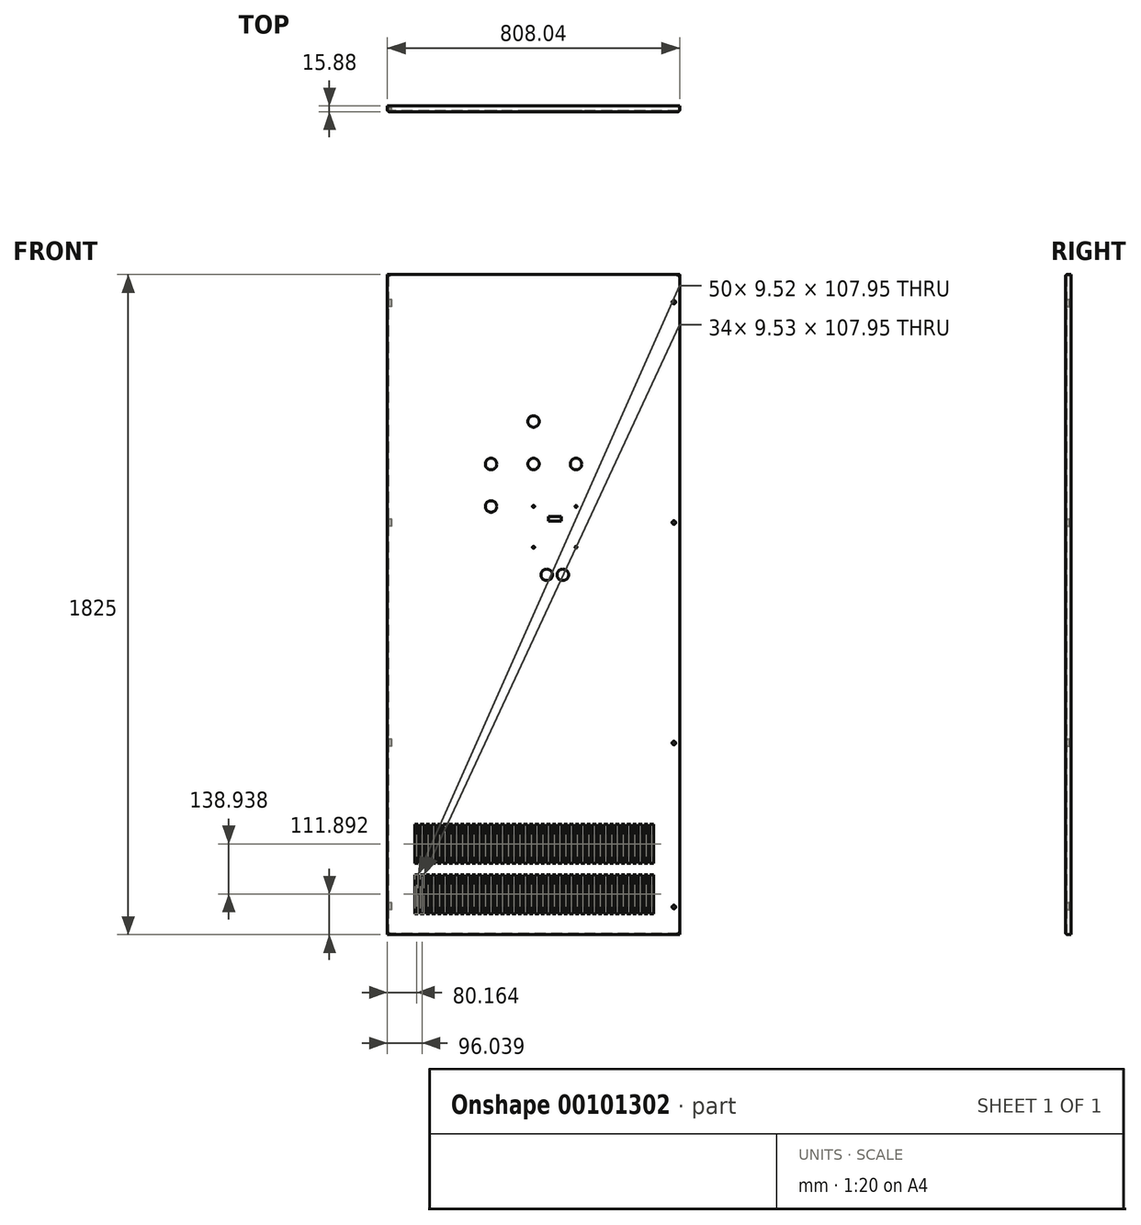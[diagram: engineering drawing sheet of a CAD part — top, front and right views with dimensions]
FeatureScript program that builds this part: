
annotation { "Feature Type Name" : "Feature", "Feature Type Description" : "" }
export const myFeature = defineFeature(function(context is Context, id is Id, definition is map)
    precondition{}
    {
        {
            var Q0;
            Q0=qCreatedBy(makeId("Front.planeOp"),FACE);
            var sketch = newSketch(context, id + "F0", { "sketchPlane" : qUnion([Q0])});
            skLineSegment(sketch, "E0.bottom", {"start": v(404.02, 912.5) * mm, "end": v(-404.02, 912.5) * mm});
            skLineSegment(sketch, "E0.top", {"start": v(404.02, -912.5) * mm, "end": v(-404.02, -912.5) * mm});
            skLineSegment(sketch, "E0.left", {"start": v(404.02, 912.5) * mm, "end": v(404.02, -912.5) * mm});
            skLineSegment(sketch, "E0.right", {"start": v(-404.02, 912.5) * mm, "end": v(-404.02, -912.5) * mm});
            skPoint(sketch, "E0.middle", {"position": v(0, 0) * mm});
            skSolve(sketch);
        }
        {
            var Q0;
            Q0=makeQuery(id+"F0.imprint","IMPRINT",FACE,{"disambiguationData":[TD([[makeQuery(id+"F0.imprint","IMPRINT",EDGE,{"derivedFrom":sQuery(id+"F0.wireOp",EDGE,"E0.bottom")}),1.0]])]});
            var Q1;
            Q1=qSketchRegion(id+"F0",true);
            extrude(context, id + "F1", {"entities" : qUnion([Q0, Q1]), "endBound" : BoundingType.SYMMETRIC, "depth" : 15.88 * mm});
        }
        {
            var Q0;
            Q0=makeQuery(id+"F1.opExtrude","CAP_FACE",FACE,{"disambiguationData":[OSD([sQuery(id+"F0.wireOp",EDGE,"E0.bottom"),sQuery(id+"F0.wireOp",EDGE,"E0.top"),sQuery(id+"F0.wireOp",EDGE,"E0.left"),sQuery(id+"F0.wireOp",EDGE,"E0.right")])],"isStart":true});
            shell(context, id + "F2", {"entities" : qUnion([Q0]), "thickness" : 2.66 * mm});
        }
        {
            var Q0;
            Q0=makeQuery(id+"F1.opExtrude","CAP_EDGE",EDGE,{"disambiguationData":[OSD([sQuery(id+"F0.wireOp",EDGE,"E0.bottom")])],"isStart":false});
            var Q1;
            Q1=makeQuery(id+"F1.opExtrude","CAP_EDGE",EDGE,{"disambiguationData":[OSD([sQuery(id+"F0.wireOp",EDGE,"E0.left")])],"isStart":false});
            var Q2;
            Q2=makeQuery(id+"F1.opExtrude","CAP_EDGE",EDGE,{"disambiguationData":[OSD([sQuery(id+"F0.wireOp",EDGE,"E0.right")])],"isStart":false});
            var Q3;
            Q3=makeQuery(id+"F1.opExtrude","CAP_EDGE",EDGE,{"disambiguationData":[OSD([sQuery(id+"F0.wireOp",EDGE,"E0.top")])],"isStart":false});
            fillet(context, id + "F3", {"entities" : qUnion([Q0, Q1, Q2, Q3]), "radius" : 5.08 * mm, "tangentPropagation" : true, "allowEdgeOverflow" : false});
        }
        {
            var Q0;
            Q0=makeQuery(id+"F1.opExtrude","CAP_FACE",FACE,{"disambiguationData":[OSD([sQuery(id+"F0.wireOp",EDGE,"E0.bottom"),sQuery(id+"F0.wireOp",EDGE,"E0.top"),sQuery(id+"F0.wireOp",EDGE,"E0.left"),sQuery(id+"F0.wireOp",EDGE,"E0.right")])],"isStart":false});
            var sketch = newSketch(context, id + "F4", { "sketchPlane" : qUnion([Q0])});
            skCircle(sketch, "E1", {"center": v(388.14, 836.3) * mm, "radius": 4.76 * mm});
            skCircle(sketch, "E2", {"center": v(388.14, -382.9) * mm, "radius": 4.76 * mm});
            skCircle(sketch, "E3", {"center": v(388.14, -836.3) * mm, "radius": 4.76 * mm});
            skLineSegment(sketch, "E4.bottom", {"start": v(322.26, -854.58) * mm, "end": v(331.78, -854.58) * mm});
            skLineSegment(sketch, "E4.top", {"start": v(322.26, -746.63) * mm, "end": v(331.78, -746.63) * mm});
            skLineSegment(sketch, "E4.left", {"start": v(322.26, -854.58) * mm, "end": v(322.26, -746.63) * mm});
            skLineSegment(sketch, "E4.right", {"start": v(331.78, -854.58) * mm, "end": v(331.78, -746.63) * mm});
            skLineSegment(sketch, "E5.1.0.0", {"start": v(315.9, -854.58) * mm, "end": v(315.9, -746.63) * mm});
            skLineSegment(sketch, "E5.1.0.1", {"start": v(306.38, -854.58) * mm, "end": v(306.38, -746.63) * mm});
            skLineSegment(sketch, "E5.1.0.2", {"start": v(306.38, -854.58) * mm, "end": v(315.9, -854.58) * mm});
            skLineSegment(sketch, "E5.1.0.3", {"start": v(306.38, -746.63) * mm, "end": v(315.9, -746.63) * mm});
            skLineSegment(sketch, "E5.2.0.0", {"start": v(300.03, -854.58) * mm, "end": v(300.03, -746.63) * mm});
            skLineSegment(sketch, "E5.2.0.1", {"start": v(290.5, -854.58) * mm, "end": v(290.5, -746.63) * mm});
            skLineSegment(sketch, "E5.2.0.2", {"start": v(290.5, -854.58) * mm, "end": v(300.03, -854.58) * mm});
            skLineSegment(sketch, "E5.2.0.3", {"start": v(290.5, -746.63) * mm, "end": v(300.03, -746.63) * mm});
            skLineSegment(sketch, "E5.3.0.0", {"start": v(284.16, -854.58) * mm, "end": v(284.16, -746.63) * mm});
            skLineSegment(sketch, "E5.3.0.1", {"start": v(274.63, -854.58) * mm, "end": v(274.63, -746.63) * mm});
            skLineSegment(sketch, "E5.3.0.2", {"start": v(274.63, -854.58) * mm, "end": v(284.16, -854.58) * mm});
            skLineSegment(sketch, "E5.3.0.3", {"start": v(274.63, -746.63) * mm, "end": v(284.16, -746.63) * mm});
            skLineSegment(sketch, "E5.4.0.0", {"start": v(268.28, -854.58) * mm, "end": v(268.28, -746.63) * mm});
            skLineSegment(sketch, "E5.4.0.1", {"start": v(258.76, -854.58) * mm, "end": v(258.76, -746.63) * mm});
            skLineSegment(sketch, "E5.4.0.2", {"start": v(258.76, -854.58) * mm, "end": v(268.28, -854.58) * mm});
            skLineSegment(sketch, "E5.4.0.3", {"start": v(258.76, -746.63) * mm, "end": v(268.28, -746.63) * mm});
            skLineSegment(sketch, "E5.5.0.0", {"start": v(252.4, -854.58) * mm, "end": v(252.4, -746.63) * mm});
            skLineSegment(sketch, "E5.5.0.1", {"start": v(242.88, -854.58) * mm, "end": v(242.88, -746.63) * mm});
            skLineSegment(sketch, "E5.5.0.2", {"start": v(242.88, -854.58) * mm, "end": v(252.4, -854.58) * mm});
            skLineSegment(sketch, "E5.5.0.3", {"start": v(242.88, -746.63) * mm, "end": v(252.4, -746.63) * mm});
            skLineSegment(sketch, "E5.6.0.0", {"start": v(236.53, -854.58) * mm, "end": v(236.53, -746.63) * mm});
            skLineSegment(sketch, "E5.6.0.1", {"start": v(227, -854.58) * mm, "end": v(227, -746.63) * mm});
            skLineSegment(sketch, "E5.6.0.2", {"start": v(227, -854.58) * mm, "end": v(236.53, -854.58) * mm});
            skLineSegment(sketch, "E5.6.0.3", {"start": v(227, -746.63) * mm, "end": v(236.53, -746.63) * mm});
            skLineSegment(sketch, "E5.7.0.0", {"start": v(220.66, -854.58) * mm, "end": v(220.66, -746.63) * mm});
            skLineSegment(sketch, "E5.7.0.1", {"start": v(211.13, -854.58) * mm, "end": v(211.13, -746.63) * mm});
            skLineSegment(sketch, "E5.7.0.2", {"start": v(211.13, -854.58) * mm, "end": v(220.66, -854.58) * mm});
            skLineSegment(sketch, "E5.7.0.3", {"start": v(211.13, -746.63) * mm, "end": v(220.66, -746.63) * mm});
            skLineSegment(sketch, "E5.8.0.0", {"start": v(204.78, -854.58) * mm, "end": v(204.78, -746.63) * mm});
            skLineSegment(sketch, "E5.8.0.1", {"start": v(195.26, -854.58) * mm, "end": v(195.26, -746.63) * mm});
            skLineSegment(sketch, "E5.8.0.2", {"start": v(195.26, -854.58) * mm, "end": v(204.78, -854.58) * mm});
            skLineSegment(sketch, "E5.8.0.3", {"start": v(195.26, -746.63) * mm, "end": v(204.78, -746.63) * mm});
            skLineSegment(sketch, "E5.9.0.0", {"start": v(188.9, -854.58) * mm, "end": v(188.9, -746.63) * mm});
            skLineSegment(sketch, "E5.9.0.1", {"start": v(179.38, -854.58) * mm, "end": v(179.38, -746.63) * mm});
            skLineSegment(sketch, "E5.9.0.2", {"start": v(179.38, -854.58) * mm, "end": v(188.9, -854.58) * mm});
            skLineSegment(sketch, "E5.9.0.3", {"start": v(179.38, -746.63) * mm, "end": v(188.9, -746.63) * mm});
            skLineSegment(sketch, "E5.10.0.0", {"start": v(173.03, -854.58) * mm, "end": v(173.03, -746.63) * mm});
            skLineSegment(sketch, "E5.10.0.1", {"start": v(163.5, -854.58) * mm, "end": v(163.5, -746.63) * mm});
            skLineSegment(sketch, "E5.10.0.2", {"start": v(163.5, -854.58) * mm, "end": v(173.03, -854.58) * mm});
            skLineSegment(sketch, "E5.10.0.3", {"start": v(163.5, -746.63) * mm, "end": v(173.03, -746.63) * mm});
            skLineSegment(sketch, "E5.11.0.0", {"start": v(157.16, -854.58) * mm, "end": v(157.16, -746.63) * mm});
            skLineSegment(sketch, "E5.11.0.1", {"start": v(147.63, -854.58) * mm, "end": v(147.63, -746.63) * mm});
            skLineSegment(sketch, "E5.11.0.2", {"start": v(147.63, -854.58) * mm, "end": v(157.16, -854.58) * mm});
            skLineSegment(sketch, "E5.11.0.3", {"start": v(147.63, -746.63) * mm, "end": v(157.16, -746.63) * mm});
            skLineSegment(sketch, "E5.12.0.0", {"start": v(141.28, -854.58) * mm, "end": v(141.28, -746.63) * mm});
            skLineSegment(sketch, "E5.12.0.1", {"start": v(131.76, -854.58) * mm, "end": v(131.76, -746.63) * mm});
            skLineSegment(sketch, "E5.12.0.2", {"start": v(131.76, -854.58) * mm, "end": v(141.28, -854.58) * mm});
            skLineSegment(sketch, "E5.12.0.3", {"start": v(131.76, -746.63) * mm, "end": v(141.28, -746.63) * mm});
            skLineSegment(sketch, "E5.13.0.0", {"start": v(125.4, -854.58) * mm, "end": v(125.4, -746.63) * mm});
            skLineSegment(sketch, "E5.13.0.1", {"start": v(115.88, -854.58) * mm, "end": v(115.88, -746.63) * mm});
            skLineSegment(sketch, "E5.13.0.2", {"start": v(115.88, -854.58) * mm, "end": v(125.4, -854.58) * mm});
            skLineSegment(sketch, "E5.13.0.3", {"start": v(115.88, -746.63) * mm, "end": v(125.4, -746.63) * mm});
            skLineSegment(sketch, "E5.14.0.0", {"start": v(109.53, -854.58) * mm, "end": v(109.53, -746.63) * mm});
            skLineSegment(sketch, "E5.14.0.1", {"start": v(100, -854.58) * mm, "end": v(100, -746.63) * mm});
            skLineSegment(sketch, "E5.14.0.2", {"start": v(100, -854.58) * mm, "end": v(109.53, -854.58) * mm});
            skLineSegment(sketch, "E5.14.0.3", {"start": v(100, -746.63) * mm, "end": v(109.53, -746.63) * mm});
            skLineSegment(sketch, "E5.15.0.0", {"start": v(93.66, -854.58) * mm, "end": v(93.66, -746.63) * mm});
            skLineSegment(sketch, "E5.15.0.1", {"start": v(84.13, -854.58) * mm, "end": v(84.13, -746.63) * mm});
            skLineSegment(sketch, "E5.15.0.2", {"start": v(84.13, -854.58) * mm, "end": v(93.66, -854.58) * mm});
            skLineSegment(sketch, "E5.15.0.3", {"start": v(84.13, -746.63) * mm, "end": v(93.66, -746.63) * mm});
            skLineSegment(sketch, "E5.16.0.0", {"start": v(77.78, -854.58) * mm, "end": v(77.78, -746.63) * mm});
            skLineSegment(sketch, "E5.16.0.1", {"start": v(68.26, -854.58) * mm, "end": v(68.26, -746.63) * mm});
            skLineSegment(sketch, "E5.16.0.2", {"start": v(68.26, -854.58) * mm, "end": v(77.78, -854.58) * mm});
            skLineSegment(sketch, "E5.16.0.3", {"start": v(68.26, -746.63) * mm, "end": v(77.78, -746.63) * mm});
            skLineSegment(sketch, "E5.17.0.0", {"start": v(61.9, -854.58) * mm, "end": v(61.9, -746.63) * mm});
            skLineSegment(sketch, "E5.17.0.1", {"start": v(52.38, -854.58) * mm, "end": v(52.38, -746.63) * mm});
            skLineSegment(sketch, "E5.17.0.2", {"start": v(52.38, -854.58) * mm, "end": v(61.9, -854.58) * mm});
            skLineSegment(sketch, "E5.17.0.3", {"start": v(52.38, -746.63) * mm, "end": v(61.9, -746.63) * mm});
            skLineSegment(sketch, "E5.18.0.0", {"start": v(46.03, -854.58) * mm, "end": v(46.03, -746.63) * mm});
            skLineSegment(sketch, "E5.18.0.1", {"start": v(36.5, -854.58) * mm, "end": v(36.5, -746.63) * mm});
            skLineSegment(sketch, "E5.18.0.2", {"start": v(36.5, -854.58) * mm, "end": v(46.03, -854.58) * mm});
            skLineSegment(sketch, "E5.18.0.3", {"start": v(36.5, -746.63) * mm, "end": v(46.03, -746.63) * mm});
            skLineSegment(sketch, "E5.19.0.0", {"start": v(30.16, -854.58) * mm, "end": v(30.16, -746.63) * mm});
            skLineSegment(sketch, "E5.19.0.1", {"start": v(20.63, -854.58) * mm, "end": v(20.63, -746.63) * mm});
            skLineSegment(sketch, "E5.19.0.2", {"start": v(20.63, -854.58) * mm, "end": v(30.16, -854.58) * mm});
            skLineSegment(sketch, "E5.19.0.3", {"start": v(20.63, -746.63) * mm, "end": v(30.16, -746.63) * mm});
            skLineSegment(sketch, "E5.20.0.0", {"start": v(14.28, -854.58) * mm, "end": v(14.28, -746.63) * mm});
            skLineSegment(sketch, "E5.20.0.1", {"start": v(4.76, -854.58) * mm, "end": v(4.76, -746.63) * mm});
            skLineSegment(sketch, "E5.20.0.2", {"start": v(4.76, -854.58) * mm, "end": v(14.28, -854.58) * mm});
            skLineSegment(sketch, "E5.20.0.3", {"start": v(4.76, -746.63) * mm, "end": v(14.28, -746.63) * mm});
            skLineSegment(sketch, "E5.21.0.0", {"start": v(-1.6, -854.58) * mm, "end": v(-1.6, -746.63) * mm});
            skLineSegment(sketch, "E5.21.0.1", {"start": v(-11.12, -854.58) * mm, "end": v(-11.12, -746.63) * mm});
            skLineSegment(sketch, "E5.21.0.2", {"start": v(-11.12, -854.58) * mm, "end": v(-1.6, -854.58) * mm});
            skLineSegment(sketch, "E5.21.0.3", {"start": v(-11.12, -746.63) * mm, "end": v(-1.6, -746.63) * mm});
            skLineSegment(sketch, "E5.22.0.0", {"start": v(-17.47, -854.58) * mm, "end": v(-17.47, -746.63) * mm});
            skLineSegment(sketch, "E5.22.0.1", {"start": v(-27, -854.58) * mm, "end": v(-27, -746.63) * mm});
            skLineSegment(sketch, "E5.22.0.2", {"start": v(-27, -854.58) * mm, "end": v(-17.47, -854.58) * mm});
            skLineSegment(sketch, "E5.22.0.3", {"start": v(-27, -746.63) * mm, "end": v(-17.47, -746.63) * mm});
            skLineSegment(sketch, "E5.23.0.0", {"start": v(-33.34, -854.58) * mm, "end": v(-33.34, -746.63) * mm});
            skLineSegment(sketch, "E5.23.0.1", {"start": v(-42.87, -854.58) * mm, "end": v(-42.87, -746.63) * mm});
            skLineSegment(sketch, "E5.23.0.2", {"start": v(-42.87, -854.58) * mm, "end": v(-33.34, -854.58) * mm});
            skLineSegment(sketch, "E5.23.0.3", {"start": v(-42.87, -746.63) * mm, "end": v(-33.34, -746.63) * mm});
            skLineSegment(sketch, "E5.24.0.0", {"start": v(-49.22, -854.58) * mm, "end": v(-49.22, -746.63) * mm});
            skLineSegment(sketch, "E5.24.0.1", {"start": v(-58.74, -854.58) * mm, "end": v(-58.74, -746.63) * mm});
            skLineSegment(sketch, "E5.24.0.2", {"start": v(-58.74, -854.58) * mm, "end": v(-49.22, -854.58) * mm});
            skLineSegment(sketch, "E5.24.0.3", {"start": v(-58.74, -746.63) * mm, "end": v(-49.22, -746.63) * mm});
            skLineSegment(sketch, "E5.25.0.0", {"start": v(-65.1, -854.58) * mm, "end": v(-65.1, -746.63) * mm});
            skLineSegment(sketch, "E5.25.0.1", {"start": v(-74.62, -854.58) * mm, "end": v(-74.62, -746.63) * mm});
            skLineSegment(sketch, "E5.25.0.2", {"start": v(-74.62, -854.58) * mm, "end": v(-65.1, -854.58) * mm});
            skLineSegment(sketch, "E5.25.0.3", {"start": v(-74.62, -746.63) * mm, "end": v(-65.1, -746.63) * mm});
            skLineSegment(sketch, "E5.26.0.0", {"start": v(-80.97, -854.58) * mm, "end": v(-80.97, -746.63) * mm});
            skLineSegment(sketch, "E5.26.0.1", {"start": v(-90.5, -854.58) * mm, "end": v(-90.5, -746.63) * mm});
            skLineSegment(sketch, "E5.26.0.2", {"start": v(-90.5, -854.58) * mm, "end": v(-80.97, -854.58) * mm});
            skLineSegment(sketch, "E5.26.0.3", {"start": v(-90.5, -746.63) * mm, "end": v(-80.97, -746.63) * mm});
            skLineSegment(sketch, "E5.27.0.0", {"start": v(-96.84, -854.58) * mm, "end": v(-96.84, -746.63) * mm});
            skLineSegment(sketch, "E5.27.0.1", {"start": v(-106.37, -854.58) * mm, "end": v(-106.37, -746.63) * mm});
            skLineSegment(sketch, "E5.27.0.2", {"start": v(-106.37, -854.58) * mm, "end": v(-96.84, -854.58) * mm});
            skLineSegment(sketch, "E5.27.0.3", {"start": v(-106.37, -746.63) * mm, "end": v(-96.84, -746.63) * mm});
            skLineSegment(sketch, "E5.28.0.0", {"start": v(-112.72, -854.58) * mm, "end": v(-112.72, -746.63) * mm});
            skLineSegment(sketch, "E5.28.0.1", {"start": v(-122.24, -854.58) * mm, "end": v(-122.24, -746.63) * mm});
            skLineSegment(sketch, "E5.28.0.2", {"start": v(-122.24, -854.58) * mm, "end": v(-112.72, -854.58) * mm});
            skLineSegment(sketch, "E5.28.0.3", {"start": v(-122.24, -746.63) * mm, "end": v(-112.72, -746.63) * mm});
            skLineSegment(sketch, "E5.29.0.0", {"start": v(-128.6, -854.58) * mm, "end": v(-128.6, -746.63) * mm});
            skLineSegment(sketch, "E5.29.0.1", {"start": v(-138.12, -854.58) * mm, "end": v(-138.12, -746.63) * mm});
            skLineSegment(sketch, "E5.29.0.2", {"start": v(-138.12, -854.58) * mm, "end": v(-128.6, -854.58) * mm});
            skLineSegment(sketch, "E5.29.0.3", {"start": v(-138.12, -746.63) * mm, "end": v(-128.6, -746.63) * mm});
            skLineSegment(sketch, "E5.30.0.0", {"start": v(-144.47, -854.58) * mm, "end": v(-144.47, -746.63) * mm});
            skLineSegment(sketch, "E5.30.0.1", {"start": v(-154, -854.58) * mm, "end": v(-154, -746.63) * mm});
            skLineSegment(sketch, "E5.30.0.2", {"start": v(-154, -854.58) * mm, "end": v(-144.47, -854.58) * mm});
            skLineSegment(sketch, "E5.30.0.3", {"start": v(-154, -746.63) * mm, "end": v(-144.47, -746.63) * mm});
            skLineSegment(sketch, "E5.31.0.0", {"start": v(-160.34, -854.58) * mm, "end": v(-160.34, -746.63) * mm});
            skLineSegment(sketch, "E5.31.0.1", {"start": v(-169.87, -854.58) * mm, "end": v(-169.87, -746.63) * mm});
            skLineSegment(sketch, "E5.31.0.2", {"start": v(-169.87, -854.58) * mm, "end": v(-160.34, -854.58) * mm});
            skLineSegment(sketch, "E5.31.0.3", {"start": v(-169.87, -746.63) * mm, "end": v(-160.34, -746.63) * mm});
            skLineSegment(sketch, "E5.32.0.0", {"start": v(-176.22, -854.58) * mm, "end": v(-176.22, -746.63) * mm});
            skLineSegment(sketch, "E5.32.0.1", {"start": v(-185.74, -854.58) * mm, "end": v(-185.74, -746.63) * mm});
            skLineSegment(sketch, "E5.32.0.2", {"start": v(-185.74, -854.58) * mm, "end": v(-176.22, -854.58) * mm});
            skLineSegment(sketch, "E5.32.0.3", {"start": v(-185.74, -746.63) * mm, "end": v(-176.22, -746.63) * mm});
            skLineSegment(sketch, "E5.33.0.0", {"start": v(-192.1, -854.58) * mm, "end": v(-192.1, -746.63) * mm});
            skLineSegment(sketch, "E5.33.0.1", {"start": v(-201.62, -854.58) * mm, "end": v(-201.62, -746.63) * mm});
            skLineSegment(sketch, "E5.33.0.2", {"start": v(-201.62, -854.58) * mm, "end": v(-192.1, -854.58) * mm});
            skLineSegment(sketch, "E5.33.0.3", {"start": v(-201.62, -746.63) * mm, "end": v(-192.1, -746.63) * mm});
            skLineSegment(sketch, "E5.direction1", {"start": v(331.78, -854.58) * mm, "end": v(315.9, -854.58) * mm, "construction": true});
            skLineSegment(sketch, "E5.direction2", {"start": v(331.78, -854.58) * mm, "end": v(331.78, -715.65) * mm, "construction": true});
            skLineSegment(sketch, "E6.0.34.0", {"start": v(-207.97, -854.58) * mm, "end": v(-207.97, -746.63) * mm});
            skLineSegment(sketch, "E6.3.34.0", {"start": v(-217.5, -854.58) * mm, "end": v(-217.5, -746.63) * mm});
            skLineSegment(sketch, "E6.6.34.0", {"start": v(-217.5, -854.58) * mm, "end": v(-207.97, -854.58) * mm});
            skLineSegment(sketch, "E6.9.34.0", {"start": v(-217.5, -746.63) * mm, "end": v(-207.97, -746.63) * mm});
            skLineSegment(sketch, "E6.0.35.0", {"start": v(-223.84, -854.58) * mm, "end": v(-223.84, -746.63) * mm});
            skLineSegment(sketch, "E6.3.35.0", {"start": v(-233.37, -854.58) * mm, "end": v(-233.37, -746.63) * mm});
            skLineSegment(sketch, "E6.6.35.0", {"start": v(-233.37, -854.58) * mm, "end": v(-223.84, -854.58) * mm});
            skLineSegment(sketch, "E6.9.35.0", {"start": v(-233.37, -746.63) * mm, "end": v(-223.84, -746.63) * mm});
            skLineSegment(sketch, "E6.0.36.0", {"start": v(-239.72, -854.58) * mm, "end": v(-239.72, -746.63) * mm});
            skLineSegment(sketch, "E6.3.36.0", {"start": v(-249.24, -854.58) * mm, "end": v(-249.24, -746.63) * mm});
            skLineSegment(sketch, "E6.6.36.0", {"start": v(-249.24, -854.58) * mm, "end": v(-239.72, -854.58) * mm});
            skLineSegment(sketch, "E6.9.36.0", {"start": v(-249.24, -746.63) * mm, "end": v(-239.72, -746.63) * mm});
            skLineSegment(sketch, "E6.0.37.0", {"start": v(-255.6, -854.58) * mm, "end": v(-255.6, -746.63) * mm});
            skLineSegment(sketch, "E6.3.37.0", {"start": v(-265.12, -854.58) * mm, "end": v(-265.12, -746.63) * mm});
            skLineSegment(sketch, "E6.6.37.0", {"start": v(-265.12, -854.58) * mm, "end": v(-255.6, -854.58) * mm});
            skLineSegment(sketch, "E6.9.37.0", {"start": v(-265.12, -746.63) * mm, "end": v(-255.6, -746.63) * mm});
            skLineSegment(sketch, "E6.0.38.0", {"start": v(-271.47, -854.58) * mm, "end": v(-271.47, -746.63) * mm});
            skLineSegment(sketch, "E6.3.38.0", {"start": v(-281, -854.58) * mm, "end": v(-281, -746.63) * mm});
            skLineSegment(sketch, "E6.6.38.0", {"start": v(-281, -854.58) * mm, "end": v(-271.47, -854.58) * mm});
            skLineSegment(sketch, "E6.9.38.0", {"start": v(-281, -746.63) * mm, "end": v(-271.47, -746.63) * mm});
            skLineSegment(sketch, "E6.0.39.0", {"start": v(-287.34, -854.58) * mm, "end": v(-287.34, -746.63) * mm});
            skLineSegment(sketch, "E6.3.39.0", {"start": v(-296.87, -854.58) * mm, "end": v(-296.87, -746.63) * mm});
            skLineSegment(sketch, "E6.6.39.0", {"start": v(-296.87, -854.58) * mm, "end": v(-287.34, -854.58) * mm});
            skLineSegment(sketch, "E6.9.39.0", {"start": v(-296.87, -746.63) * mm, "end": v(-287.34, -746.63) * mm});
            skLineSegment(sketch, "E6.0.40.0", {"start": v(-303.22, -854.58) * mm, "end": v(-303.22, -746.63) * mm});
            skLineSegment(sketch, "E6.3.40.0", {"start": v(-312.74, -854.58) * mm, "end": v(-312.74, -746.63) * mm});
            skLineSegment(sketch, "E6.6.40.0", {"start": v(-312.74, -854.58) * mm, "end": v(-303.22, -854.58) * mm});
            skLineSegment(sketch, "E6.9.40.0", {"start": v(-312.74, -746.63) * mm, "end": v(-303.22, -746.63) * mm});
            skLineSegment(sketch, "E6.0.41.0", {"start": v(-319.1, -854.58) * mm, "end": v(-319.1, -746.63) * mm});
            skLineSegment(sketch, "E6.3.41.0", {"start": v(-328.62, -854.58) * mm, "end": v(-328.62, -746.63) * mm});
            skLineSegment(sketch, "E6.6.41.0", {"start": v(-328.62, -854.58) * mm, "end": v(-319.1, -854.58) * mm});
            skLineSegment(sketch, "E6.9.41.0", {"start": v(-328.62, -746.63) * mm, "end": v(-319.1, -746.63) * mm});
            skLineSegment(sketch, "E7.direction1", {"start": v(-281, -854.58) * mm, "end": v(-259.44, -854.58) * mm, "construction": true});
            skLineSegment(sketch, "E8.0.0.1", {"start": v(331.78, -715.65) * mm, "end": v(331.78, -607.7) * mm});
            skLineSegment(sketch, "E8.3.0.1", {"start": v(322.26, -715.65) * mm, "end": v(322.26, -607.7) * mm});
            skLineSegment(sketch, "E8.6.0.1", {"start": v(322.26, -715.65) * mm, "end": v(331.78, -715.65) * mm});
            skLineSegment(sketch, "E8.9.0.1", {"start": v(322.26, -607.7) * mm, "end": v(331.78, -607.7) * mm});
            skLineSegment(sketch, "E8.0.1.1", {"start": v(315.9, -715.65) * mm, "end": v(315.9, -607.7) * mm});
            skLineSegment(sketch, "E8.3.1.1", {"start": v(306.38, -715.65) * mm, "end": v(306.38, -607.7) * mm});
            skLineSegment(sketch, "E8.6.1.1", {"start": v(306.38, -715.65) * mm, "end": v(315.9, -715.65) * mm});
            skLineSegment(sketch, "E8.9.1.1", {"start": v(306.38, -607.7) * mm, "end": v(315.9, -607.7) * mm});
            skLineSegment(sketch, "E8.0.2.1", {"start": v(300.03, -715.65) * mm, "end": v(300.03, -607.7) * mm});
            skLineSegment(sketch, "E8.3.2.1", {"start": v(290.5, -715.65) * mm, "end": v(290.5, -607.7) * mm});
            skLineSegment(sketch, "E8.6.2.1", {"start": v(290.5, -715.65) * mm, "end": v(300.03, -715.65) * mm});
            skLineSegment(sketch, "E8.9.2.1", {"start": v(290.5, -607.7) * mm, "end": v(300.03, -607.7) * mm});
            skLineSegment(sketch, "E8.0.3.1", {"start": v(284.16, -715.65) * mm, "end": v(284.16, -607.7) * mm});
            skLineSegment(sketch, "E8.3.3.1", {"start": v(274.63, -715.65) * mm, "end": v(274.63, -607.7) * mm});
            skLineSegment(sketch, "E8.6.3.1", {"start": v(274.63, -715.65) * mm, "end": v(284.16, -715.65) * mm});
            skLineSegment(sketch, "E8.9.3.1", {"start": v(274.63, -607.7) * mm, "end": v(284.16, -607.7) * mm});
            skLineSegment(sketch, "E8.0.4.1", {"start": v(268.28, -715.65) * mm, "end": v(268.28, -607.7) * mm});
            skLineSegment(sketch, "E8.3.4.1", {"start": v(258.76, -715.65) * mm, "end": v(258.76, -607.7) * mm});
            skLineSegment(sketch, "E8.6.4.1", {"start": v(258.76, -715.65) * mm, "end": v(268.28, -715.65) * mm});
            skLineSegment(sketch, "E8.9.4.1", {"start": v(258.76, -607.7) * mm, "end": v(268.28, -607.7) * mm});
            skLineSegment(sketch, "E8.0.5.1", {"start": v(252.4, -715.65) * mm, "end": v(252.4, -607.7) * mm});
            skLineSegment(sketch, "E8.3.5.1", {"start": v(242.88, -715.65) * mm, "end": v(242.88, -607.7) * mm});
            skLineSegment(sketch, "E8.6.5.1", {"start": v(242.88, -715.65) * mm, "end": v(252.4, -715.65) * mm});
            skLineSegment(sketch, "E8.9.5.1", {"start": v(242.88, -607.7) * mm, "end": v(252.4, -607.7) * mm});
            skLineSegment(sketch, "E8.0.6.1", {"start": v(236.53, -715.65) * mm, "end": v(236.53, -607.7) * mm});
            skLineSegment(sketch, "E8.3.6.1", {"start": v(227, -715.65) * mm, "end": v(227, -607.7) * mm});
            skLineSegment(sketch, "E8.6.6.1", {"start": v(227, -715.65) * mm, "end": v(236.53, -715.65) * mm});
            skLineSegment(sketch, "E8.9.6.1", {"start": v(227, -607.7) * mm, "end": v(236.53, -607.7) * mm});
            skLineSegment(sketch, "E8.0.7.1", {"start": v(220.66, -715.65) * mm, "end": v(220.66, -607.7) * mm});
            skLineSegment(sketch, "E8.3.7.1", {"start": v(211.13, -715.65) * mm, "end": v(211.13, -607.7) * mm});
            skLineSegment(sketch, "E8.6.7.1", {"start": v(211.13, -715.65) * mm, "end": v(220.66, -715.65) * mm});
            skLineSegment(sketch, "E8.9.7.1", {"start": v(211.13, -607.7) * mm, "end": v(220.66, -607.7) * mm});
            skLineSegment(sketch, "E8.0.8.1", {"start": v(204.78, -715.65) * mm, "end": v(204.78, -607.7) * mm});
            skLineSegment(sketch, "E8.3.8.1", {"start": v(195.26, -715.65) * mm, "end": v(195.26, -607.7) * mm});
            skLineSegment(sketch, "E8.6.8.1", {"start": v(195.26, -715.65) * mm, "end": v(204.78, -715.65) * mm});
            skLineSegment(sketch, "E8.9.8.1", {"start": v(195.26, -607.7) * mm, "end": v(204.78, -607.7) * mm});
            skLineSegment(sketch, "E8.0.9.1", {"start": v(188.9, -715.65) * mm, "end": v(188.9, -607.7) * mm});
            skLineSegment(sketch, "E8.3.9.1", {"start": v(179.38, -715.65) * mm, "end": v(179.38, -607.7) * mm});
            skLineSegment(sketch, "E8.6.9.1", {"start": v(179.38, -715.65) * mm, "end": v(188.9, -715.65) * mm});
            skLineSegment(sketch, "E8.9.9.1", {"start": v(179.38, -607.7) * mm, "end": v(188.9, -607.7) * mm});
            skLineSegment(sketch, "E8.0.10.1", {"start": v(173.03, -715.65) * mm, "end": v(173.03, -607.7) * mm});
            skLineSegment(sketch, "E8.3.10.1", {"start": v(163.5, -715.65) * mm, "end": v(163.5, -607.7) * mm});
            skLineSegment(sketch, "E8.6.10.1", {"start": v(163.5, -715.65) * mm, "end": v(173.03, -715.65) * mm});
            skLineSegment(sketch, "E8.9.10.1", {"start": v(163.5, -607.7) * mm, "end": v(173.03, -607.7) * mm});
            skLineSegment(sketch, "E8.0.11.1", {"start": v(157.16, -715.65) * mm, "end": v(157.16, -607.7) * mm});
            skLineSegment(sketch, "E8.3.11.1", {"start": v(147.63, -715.65) * mm, "end": v(147.63, -607.7) * mm});
            skLineSegment(sketch, "E8.6.11.1", {"start": v(147.63, -715.65) * mm, "end": v(157.16, -715.65) * mm});
            skLineSegment(sketch, "E8.9.11.1", {"start": v(147.63, -607.7) * mm, "end": v(157.16, -607.7) * mm});
            skLineSegment(sketch, "E8.0.12.1", {"start": v(141.28, -715.65) * mm, "end": v(141.28, -607.7) * mm});
            skLineSegment(sketch, "E8.3.12.1", {"start": v(131.76, -715.65) * mm, "end": v(131.76, -607.7) * mm});
            skLineSegment(sketch, "E8.6.12.1", {"start": v(131.76, -715.65) * mm, "end": v(141.28, -715.65) * mm});
            skLineSegment(sketch, "E8.9.12.1", {"start": v(131.76, -607.7) * mm, "end": v(141.28, -607.7) * mm});
            skLineSegment(sketch, "E8.0.13.1", {"start": v(125.4, -715.65) * mm, "end": v(125.4, -607.7) * mm});
            skLineSegment(sketch, "E8.3.13.1", {"start": v(115.88, -715.65) * mm, "end": v(115.88, -607.7) * mm});
            skLineSegment(sketch, "E8.6.13.1", {"start": v(115.88, -715.65) * mm, "end": v(125.4, -715.65) * mm});
            skLineSegment(sketch, "E8.9.13.1", {"start": v(115.88, -607.7) * mm, "end": v(125.4, -607.7) * mm});
            skLineSegment(sketch, "E8.0.14.1", {"start": v(109.53, -715.65) * mm, "end": v(109.53, -607.7) * mm});
            skLineSegment(sketch, "E8.3.14.1", {"start": v(100, -715.65) * mm, "end": v(100, -607.7) * mm});
            skLineSegment(sketch, "E8.6.14.1", {"start": v(100, -715.65) * mm, "end": v(109.53, -715.65) * mm});
            skLineSegment(sketch, "E8.9.14.1", {"start": v(100, -607.7) * mm, "end": v(109.53, -607.7) * mm});
            skLineSegment(sketch, "E8.0.15.1", {"start": v(93.66, -715.65) * mm, "end": v(93.66, -607.7) * mm});
            skLineSegment(sketch, "E8.3.15.1", {"start": v(84.13, -715.65) * mm, "end": v(84.13, -607.7) * mm});
            skLineSegment(sketch, "E8.6.15.1", {"start": v(84.13, -715.65) * mm, "end": v(93.66, -715.65) * mm});
            skLineSegment(sketch, "E8.9.15.1", {"start": v(84.13, -607.7) * mm, "end": v(93.66, -607.7) * mm});
            skLineSegment(sketch, "E8.0.16.1", {"start": v(77.78, -715.65) * mm, "end": v(77.78, -607.7) * mm});
            skLineSegment(sketch, "E8.3.16.1", {"start": v(68.26, -715.65) * mm, "end": v(68.26, -607.7) * mm});
            skLineSegment(sketch, "E8.6.16.1", {"start": v(68.26, -715.65) * mm, "end": v(77.78, -715.65) * mm});
            skLineSegment(sketch, "E8.9.16.1", {"start": v(68.26, -607.7) * mm, "end": v(77.78, -607.7) * mm});
            skLineSegment(sketch, "E8.0.17.1", {"start": v(61.9, -715.65) * mm, "end": v(61.9, -607.7) * mm});
            skLineSegment(sketch, "E8.3.17.1", {"start": v(52.38, -715.65) * mm, "end": v(52.38, -607.7) * mm});
            skLineSegment(sketch, "E8.6.17.1", {"start": v(52.38, -715.65) * mm, "end": v(61.9, -715.65) * mm});
            skLineSegment(sketch, "E8.9.17.1", {"start": v(52.38, -607.7) * mm, "end": v(61.9, -607.7) * mm});
            skLineSegment(sketch, "E8.0.18.1", {"start": v(46.03, -715.65) * mm, "end": v(46.03, -607.7) * mm});
            skLineSegment(sketch, "E8.3.18.1", {"start": v(36.5, -715.65) * mm, "end": v(36.5, -607.7) * mm});
            skLineSegment(sketch, "E8.6.18.1", {"start": v(36.5, -715.65) * mm, "end": v(46.03, -715.65) * mm});
            skLineSegment(sketch, "E8.9.18.1", {"start": v(36.5, -607.7) * mm, "end": v(46.03, -607.7) * mm});
            skLineSegment(sketch, "E8.0.19.1", {"start": v(30.16, -715.65) * mm, "end": v(30.16, -607.7) * mm});
            skLineSegment(sketch, "E8.3.19.1", {"start": v(20.63, -715.65) * mm, "end": v(20.63, -607.7) * mm});
            skLineSegment(sketch, "E8.6.19.1", {"start": v(20.63, -715.65) * mm, "end": v(30.16, -715.65) * mm});
            skLineSegment(sketch, "E8.9.19.1", {"start": v(20.63, -607.7) * mm, "end": v(30.16, -607.7) * mm});
            skLineSegment(sketch, "E8.0.20.1", {"start": v(14.28, -715.65) * mm, "end": v(14.28, -607.7) * mm});
            skLineSegment(sketch, "E8.3.20.1", {"start": v(4.76, -715.65) * mm, "end": v(4.76, -607.7) * mm});
            skLineSegment(sketch, "E8.6.20.1", {"start": v(4.76, -715.65) * mm, "end": v(14.28, -715.65) * mm});
            skLineSegment(sketch, "E8.9.20.1", {"start": v(4.76, -607.7) * mm, "end": v(14.28, -607.7) * mm});
            skLineSegment(sketch, "E8.0.21.1", {"start": v(-1.6, -715.65) * mm, "end": v(-1.6, -607.7) * mm});
            skLineSegment(sketch, "E8.3.21.1", {"start": v(-11.12, -715.65) * mm, "end": v(-11.12, -607.7) * mm});
            skLineSegment(sketch, "E8.6.21.1", {"start": v(-11.12, -715.65) * mm, "end": v(-1.6, -715.65) * mm});
            skLineSegment(sketch, "E8.9.21.1", {"start": v(-11.12, -607.7) * mm, "end": v(-1.6, -607.7) * mm});
            skLineSegment(sketch, "E8.0.22.1", {"start": v(-17.47, -715.65) * mm, "end": v(-17.47, -607.7) * mm});
            skLineSegment(sketch, "E8.3.22.1", {"start": v(-27, -715.65) * mm, "end": v(-27, -607.7) * mm});
            skLineSegment(sketch, "E8.6.22.1", {"start": v(-27, -715.65) * mm, "end": v(-17.47, -715.65) * mm});
            skLineSegment(sketch, "E8.9.22.1", {"start": v(-27, -607.7) * mm, "end": v(-17.47, -607.7) * mm});
            skLineSegment(sketch, "E8.0.23.1", {"start": v(-33.34, -715.65) * mm, "end": v(-33.34, -607.7) * mm});
            skLineSegment(sketch, "E8.3.23.1", {"start": v(-42.87, -715.65) * mm, "end": v(-42.87, -607.7) * mm});
            skLineSegment(sketch, "E8.6.23.1", {"start": v(-42.87, -715.65) * mm, "end": v(-33.34, -715.65) * mm});
            skLineSegment(sketch, "E8.9.23.1", {"start": v(-42.87, -607.7) * mm, "end": v(-33.34, -607.7) * mm});
            skLineSegment(sketch, "E8.0.24.1", {"start": v(-49.22, -715.65) * mm, "end": v(-49.22, -607.7) * mm});
            skLineSegment(sketch, "E8.3.24.1", {"start": v(-58.74, -715.65) * mm, "end": v(-58.74, -607.7) * mm});
            skLineSegment(sketch, "E8.6.24.1", {"start": v(-58.74, -715.65) * mm, "end": v(-49.22, -715.65) * mm});
            skLineSegment(sketch, "E8.9.24.1", {"start": v(-58.74, -607.7) * mm, "end": v(-49.22, -607.7) * mm});
            skLineSegment(sketch, "E8.0.25.1", {"start": v(-65.1, -715.65) * mm, "end": v(-65.1, -607.7) * mm});
            skLineSegment(sketch, "E8.3.25.1", {"start": v(-74.62, -715.65) * mm, "end": v(-74.62, -607.7) * mm});
            skLineSegment(sketch, "E8.6.25.1", {"start": v(-74.62, -715.65) * mm, "end": v(-65.1, -715.65) * mm});
            skLineSegment(sketch, "E8.9.25.1", {"start": v(-74.62, -607.7) * mm, "end": v(-65.1, -607.7) * mm});
            skLineSegment(sketch, "E8.0.26.1", {"start": v(-80.97, -715.65) * mm, "end": v(-80.97, -607.7) * mm});
            skLineSegment(sketch, "E8.3.26.1", {"start": v(-90.5, -715.65) * mm, "end": v(-90.5, -607.7) * mm});
            skLineSegment(sketch, "E8.6.26.1", {"start": v(-90.5, -715.65) * mm, "end": v(-80.97, -715.65) * mm});
            skLineSegment(sketch, "E8.9.26.1", {"start": v(-90.5, -607.7) * mm, "end": v(-80.97, -607.7) * mm});
            skLineSegment(sketch, "E8.0.27.1", {"start": v(-96.84, -715.65) * mm, "end": v(-96.84, -607.7) * mm});
            skLineSegment(sketch, "E8.3.27.1", {"start": v(-106.37, -715.65) * mm, "end": v(-106.37, -607.7) * mm});
            skLineSegment(sketch, "E8.6.27.1", {"start": v(-106.37, -715.65) * mm, "end": v(-96.84, -715.65) * mm});
            skLineSegment(sketch, "E8.9.27.1", {"start": v(-106.37, -607.7) * mm, "end": v(-96.84, -607.7) * mm});
            skLineSegment(sketch, "E8.0.28.1", {"start": v(-112.72, -715.65) * mm, "end": v(-112.72, -607.7) * mm});
            skLineSegment(sketch, "E8.3.28.1", {"start": v(-122.24, -715.65) * mm, "end": v(-122.24, -607.7) * mm});
            skLineSegment(sketch, "E8.6.28.1", {"start": v(-122.24, -715.65) * mm, "end": v(-112.72, -715.65) * mm});
            skLineSegment(sketch, "E8.9.28.1", {"start": v(-122.24, -607.7) * mm, "end": v(-112.72, -607.7) * mm});
            skLineSegment(sketch, "E8.0.29.1", {"start": v(-128.6, -715.65) * mm, "end": v(-128.6, -607.7) * mm});
            skLineSegment(sketch, "E8.3.29.1", {"start": v(-138.12, -715.65) * mm, "end": v(-138.12, -607.7) * mm});
            skLineSegment(sketch, "E8.6.29.1", {"start": v(-138.12, -715.65) * mm, "end": v(-128.6, -715.65) * mm});
            skLineSegment(sketch, "E8.9.29.1", {"start": v(-138.12, -607.7) * mm, "end": v(-128.6, -607.7) * mm});
            skLineSegment(sketch, "E8.0.30.1", {"start": v(-144.47, -715.65) * mm, "end": v(-144.47, -607.7) * mm});
            skLineSegment(sketch, "E8.3.30.1", {"start": v(-154, -715.65) * mm, "end": v(-154, -607.7) * mm});
            skLineSegment(sketch, "E8.6.30.1", {"start": v(-154, -715.65) * mm, "end": v(-144.47, -715.65) * mm});
            skLineSegment(sketch, "E8.9.30.1", {"start": v(-154, -607.7) * mm, "end": v(-144.47, -607.7) * mm});
            skLineSegment(sketch, "E8.0.31.1", {"start": v(-160.34, -715.65) * mm, "end": v(-160.34, -607.7) * mm});
            skLineSegment(sketch, "E8.3.31.1", {"start": v(-169.87, -715.65) * mm, "end": v(-169.87, -607.7) * mm});
            skLineSegment(sketch, "E8.6.31.1", {"start": v(-169.87, -715.65) * mm, "end": v(-160.34, -715.65) * mm});
            skLineSegment(sketch, "E8.9.31.1", {"start": v(-169.87, -607.7) * mm, "end": v(-160.34, -607.7) * mm});
            skLineSegment(sketch, "E8.0.32.1", {"start": v(-176.22, -715.65) * mm, "end": v(-176.22, -607.7) * mm});
            skLineSegment(sketch, "E8.3.32.1", {"start": v(-185.74, -715.65) * mm, "end": v(-185.74, -607.7) * mm});
            skLineSegment(sketch, "E8.6.32.1", {"start": v(-185.74, -715.65) * mm, "end": v(-176.22, -715.65) * mm});
            skLineSegment(sketch, "E8.9.32.1", {"start": v(-185.74, -607.7) * mm, "end": v(-176.22, -607.7) * mm});
            skLineSegment(sketch, "E8.0.33.1", {"start": v(-192.1, -715.65) * mm, "end": v(-192.1, -607.7) * mm});
            skLineSegment(sketch, "E8.3.33.1", {"start": v(-201.62, -715.65) * mm, "end": v(-201.62, -607.7) * mm});
            skLineSegment(sketch, "E8.6.33.1", {"start": v(-201.62, -715.65) * mm, "end": v(-192.1, -715.65) * mm});
            skLineSegment(sketch, "E8.9.33.1", {"start": v(-201.62, -607.7) * mm, "end": v(-192.1, -607.7) * mm});
            skLineSegment(sketch, "E8.0.34.1", {"start": v(-207.97, -715.65) * mm, "end": v(-207.97, -607.7) * mm});
            skLineSegment(sketch, "E8.3.34.1", {"start": v(-217.5, -715.65) * mm, "end": v(-217.5, -607.7) * mm});
            skLineSegment(sketch, "E8.6.34.1", {"start": v(-217.5, -715.65) * mm, "end": v(-207.97, -715.65) * mm});
            skLineSegment(sketch, "E8.9.34.1", {"start": v(-217.5, -607.7) * mm, "end": v(-207.97, -607.7) * mm});
            skLineSegment(sketch, "E8.0.35.1", {"start": v(-223.84, -715.65) * mm, "end": v(-223.84, -607.7) * mm});
            skLineSegment(sketch, "E8.3.35.1", {"start": v(-233.37, -715.65) * mm, "end": v(-233.37, -607.7) * mm});
            skLineSegment(sketch, "E8.6.35.1", {"start": v(-233.37, -715.65) * mm, "end": v(-223.84, -715.65) * mm});
            skLineSegment(sketch, "E8.9.35.1", {"start": v(-233.37, -607.7) * mm, "end": v(-223.84, -607.7) * mm});
            skLineSegment(sketch, "E8.0.36.1", {"start": v(-239.72, -715.65) * mm, "end": v(-239.72, -607.7) * mm});
            skLineSegment(sketch, "E8.3.36.1", {"start": v(-249.24, -715.65) * mm, "end": v(-249.24, -607.7) * mm});
            skLineSegment(sketch, "E8.6.36.1", {"start": v(-249.24, -715.65) * mm, "end": v(-239.72, -715.65) * mm});
            skLineSegment(sketch, "E8.9.36.1", {"start": v(-249.24, -607.7) * mm, "end": v(-239.72, -607.7) * mm});
            skLineSegment(sketch, "E8.0.37.1", {"start": v(-255.6, -715.65) * mm, "end": v(-255.6, -607.7) * mm});
            skLineSegment(sketch, "E8.3.37.1", {"start": v(-265.12, -715.65) * mm, "end": v(-265.12, -607.7) * mm});
            skLineSegment(sketch, "E8.6.37.1", {"start": v(-265.12, -715.65) * mm, "end": v(-255.6, -715.65) * mm});
            skLineSegment(sketch, "E8.9.37.1", {"start": v(-265.12, -607.7) * mm, "end": v(-255.6, -607.7) * mm});
            skLineSegment(sketch, "E8.0.38.1", {"start": v(-271.47, -715.65) * mm, "end": v(-271.47, -607.7) * mm});
            skLineSegment(sketch, "E8.3.38.1", {"start": v(-281, -715.65) * mm, "end": v(-281, -607.7) * mm});
            skLineSegment(sketch, "E8.6.38.1", {"start": v(-281, -715.65) * mm, "end": v(-271.47, -715.65) * mm});
            skLineSegment(sketch, "E8.9.38.1", {"start": v(-281, -607.7) * mm, "end": v(-271.47, -607.7) * mm});
            skLineSegment(sketch, "E8.0.39.1", {"start": v(-287.34, -715.65) * mm, "end": v(-287.34, -607.7) * mm});
            skLineSegment(sketch, "E8.3.39.1", {"start": v(-296.87, -715.65) * mm, "end": v(-296.87, -607.7) * mm});
            skLineSegment(sketch, "E8.6.39.1", {"start": v(-296.87, -715.65) * mm, "end": v(-287.34, -715.65) * mm});
            skLineSegment(sketch, "E8.9.39.1", {"start": v(-296.87, -607.7) * mm, "end": v(-287.34, -607.7) * mm});
            skLineSegment(sketch, "E8.0.40.1", {"start": v(-303.22, -715.65) * mm, "end": v(-303.22, -607.7) * mm});
            skLineSegment(sketch, "E8.3.40.1", {"start": v(-312.74, -715.65) * mm, "end": v(-312.74, -607.7) * mm});
            skLineSegment(sketch, "E8.6.40.1", {"start": v(-312.74, -715.65) * mm, "end": v(-303.22, -715.65) * mm});
            skLineSegment(sketch, "E8.9.40.1", {"start": v(-312.74, -607.7) * mm, "end": v(-303.22, -607.7) * mm});
            skLineSegment(sketch, "E8.0.41.1", {"start": v(-319.1, -715.65) * mm, "end": v(-319.1, -607.7) * mm});
            skLineSegment(sketch, "E8.3.41.1", {"start": v(-328.62, -715.65) * mm, "end": v(-328.62, -607.7) * mm});
            skLineSegment(sketch, "E8.6.41.1", {"start": v(-328.62, -715.65) * mm, "end": v(-319.1, -715.65) * mm});
            skLineSegment(sketch, "E8.9.41.1", {"start": v(-328.62, -607.7) * mm, "end": v(-319.1, -607.7) * mm});
            skCircle(sketch, "E9", {"center": v(388.14, 226.7) * mm, "radius": 4.76 * mm});
            skCircle(sketch, "E10", {"center": v(0, 388.62) * mm, "radius": 15.88 * mm});
            skCircle(sketch, "E11", {"center": v(117.47, 388.62) * mm, "radius": 15.88 * mm});
            skCircle(sketch, "E12", {"center": v(-117.47, 388.62) * mm, "radius": 15.88 * mm});
            skCircle(sketch, "E13", {"center": v(0, 506.1) * mm, "radius": 15.88 * mm});
            skCircle(sketch, "E14", {"center": v(-117.48, 271.15) * mm, "radius": 15.88 * mm});
            skLineSegment(sketch, "E15", {"start": v(-117.47, 388.62) * mm, "end": v(0, 388.62) * mm, "construction": true});
            skLineSegment(sketch, "E16", {"start": v(0, 506.1) * mm, "end": v(0, 388.62) * mm, "construction": true});
            skLineSegment(sketch, "E17", {"start": v(0, 388.62) * mm, "end": v(117.47, 388.62) * mm, "construction": true});
            skLineSegment(sketch, "E18", {"start": v(-117.48, 388.62) * mm, "end": v(-117.48, 271.15) * mm, "construction": true});
            skLineSegment(sketch, "E19.bottom", {"start": v(41.02, 243.64) * mm, "end": v(76.58, 243.64) * mm});
            skLineSegment(sketch, "E19.top", {"start": v(41.02, 230.94) * mm, "end": v(76.58, 230.94) * mm});
            skLineSegment(sketch, "E19.left", {"start": v(41.02, 243.64) * mm, "end": v(41.02, 230.94) * mm});
            skLineSegment(sketch, "E19.right", {"start": v(76.58, 243.64) * mm, "end": v(76.58, 230.94) * mm});
            skPoint(sketch, "E19.middle", {"position": v(58.8, 237.29) * mm});
            skLineSegment(sketch, "E20.bottom", {"start": v(0, 271.15) * mm, "end": v(117.6, 271.15) * mm, "construction": true});
            skLineSegment(sketch, "E20.top", {"start": v(0, 158.37) * mm, "end": v(117.6, 158.37) * mm, "construction": true});
            skLineSegment(sketch, "E20.left", {"start": v(0, 271.15) * mm, "end": v(0, 158.37) * mm, "construction": true});
            skLineSegment(sketch, "E20.right", {"start": v(117.6, 271.15) * mm, "end": v(117.6, 158.37) * mm, "construction": true});
            skCircle(sketch, "E21", {"center": v(0, 271.15) * mm, "radius": 2.77 * mm});
            skCircle(sketch, "E22", {"center": v(117.6, 271.15) * mm, "radius": 2.77 * mm});
            skCircle(sketch, "E23", {"center": v(117.6, 158.37) * mm, "radius": 2.77 * mm});
            skCircle(sketch, "E24", {"center": v(0, 158.37) * mm, "radius": 2.77 * mm});
            skCircle(sketch, "E25", {"center": v(36.58, 82.17) * mm, "radius": 15.88 * mm});
            skCircle(sketch, "E26", {"center": v(81.03, 82.17) * mm, "radius": 15.88 * mm});
            skLineSegment(sketch, "E27", {"start": v(36.58, 82.17) * mm, "end": v(81.03, 82.17) * mm, "construction": true});
            skPoint(sketch, "E28", {"position": v(58.8, 82.17) * mm});
            skSolve(sketch);
        }
        {
            var Q0;
            Q0=qSketchRegion(id+"F4",true);
            extrude(context, id + "F5", {"entities" : qUnion([Q0]), "operationType" : NewBodyOperationType.REMOVE, "endBound" : BoundingType.THROUGH_ALL, "oppositeDirection" : true, "depth" : 25.4 * mm});
        }
        {
            var Q0;
            Q0=makeQuery(id+"F2.opShell","OFFSET_FACE",FACE,{"disambiguationData":[OSD([sQuery(id+"F0.wireOp",EDGE,"E0.right")])]});
            cPlane(context, id + "F6", {"entities" : qUnion([Q0]), "cplaneType" : CPlaneType.OFFSET, "offset" : 4.76 * mm, "width" : 152.4 * mm, "height" : 152.4 * mm});
        }
        {
            var Q0;
            Q0=qCreatedBy(id+"F6.planeOp",FACE);
            var sketch = newSketch(context, id + "F7", { "sketchPlane" : qUnion([Q0])});
            skLineSegment(sketch, "E29", {"start": v(-0.52, 909.84) * mm, "end": v(-0.52, -909.84) * mm, "construction": true});
            skLineSegment(sketch, "E30.bottom", {"start": v(-5.28, 824.11) * mm, "end": v(-3.7, 824.11) * mm});
            skLineSegment(sketch, "E30.top", {"start": v(-5.28, 843.16) * mm, "end": v(-3.7, 843.16) * mm});
            skLineSegment(sketch, "E30.left", {"start": v(-5.28, 824.11) * mm, "end": v(-5.28, 843.16) * mm});
            skLineSegment(sketch, "E30.right", {"start": v(-3.7, 824.11) * mm, "end": v(-3.7, 843.16) * mm});
            skPoint(sketch, "E30.middle", {"position": v(-4.49, 833.64) * mm});
            skLineSegment(sketch, "E31.bottom", {"start": v(-5.28, 216.1) * mm, "end": v(-3.7, 216.1) * mm});
            skLineSegment(sketch, "E31.top", {"start": v(-5.28, 235.15) * mm, "end": v(-3.7, 235.15) * mm});
            skLineSegment(sketch, "E31.left", {"start": v(-5.28, 216.1) * mm, "end": v(-5.28, 235.15) * mm});
            skLineSegment(sketch, "E31.right", {"start": v(-3.7, 216.1) * mm, "end": v(-3.7, 235.15) * mm});
            skPoint(sketch, "E31.middle", {"position": v(-4.49, 225.63) * mm});
            skLineSegment(sketch, "E32.bottom", {"start": v(-5.28, -391.91) * mm, "end": v(-3.7, -391.91) * mm});
            skLineSegment(sketch, "E32.top", {"start": v(-5.28, -372.86) * mm, "end": v(-3.7, -372.86) * mm});
            skLineSegment(sketch, "E32.left", {"start": v(-5.28, -391.91) * mm, "end": v(-5.28, -372.86) * mm});
            skLineSegment(sketch, "E32.right", {"start": v(-3.7, -391.91) * mm, "end": v(-3.7, -372.86) * mm});
            skPoint(sketch, "E32.middle", {"position": v(-4.49, -382.39) * mm});
            skLineSegment(sketch, "E33.bottom", {"start": v(-5.28, -843.16) * mm, "end": v(-3.7, -843.16) * mm});
            skLineSegment(sketch, "E33.top", {"start": v(-5.28, -824.11) * mm, "end": v(-3.7, -824.11) * mm});
            skLineSegment(sketch, "E33.left", {"start": v(-5.28, -843.16) * mm, "end": v(-5.28, -824.11) * mm});
            skLineSegment(sketch, "E33.right", {"start": v(-3.7, -843.16) * mm, "end": v(-3.7, -824.11) * mm});
            skPoint(sketch, "E33.middle", {"position": v(-4.49, -833.64) * mm});
            skSolve(sketch);
        }
        {
            var Q0;
            Q0 = qSketchRegion(id + "F7", true);
            var Q1;
            Q1=sQuery(id+"F7.wireOp",EDGE,"E29");
            revolve(context, id + "F8", {"operationType" : NewBodyOperationType.ADD, "entities" : qUnion([Q0]), "axis" : qUnion([Q1]), "revolveType" : RevolveType.FULL});
        }
    });
